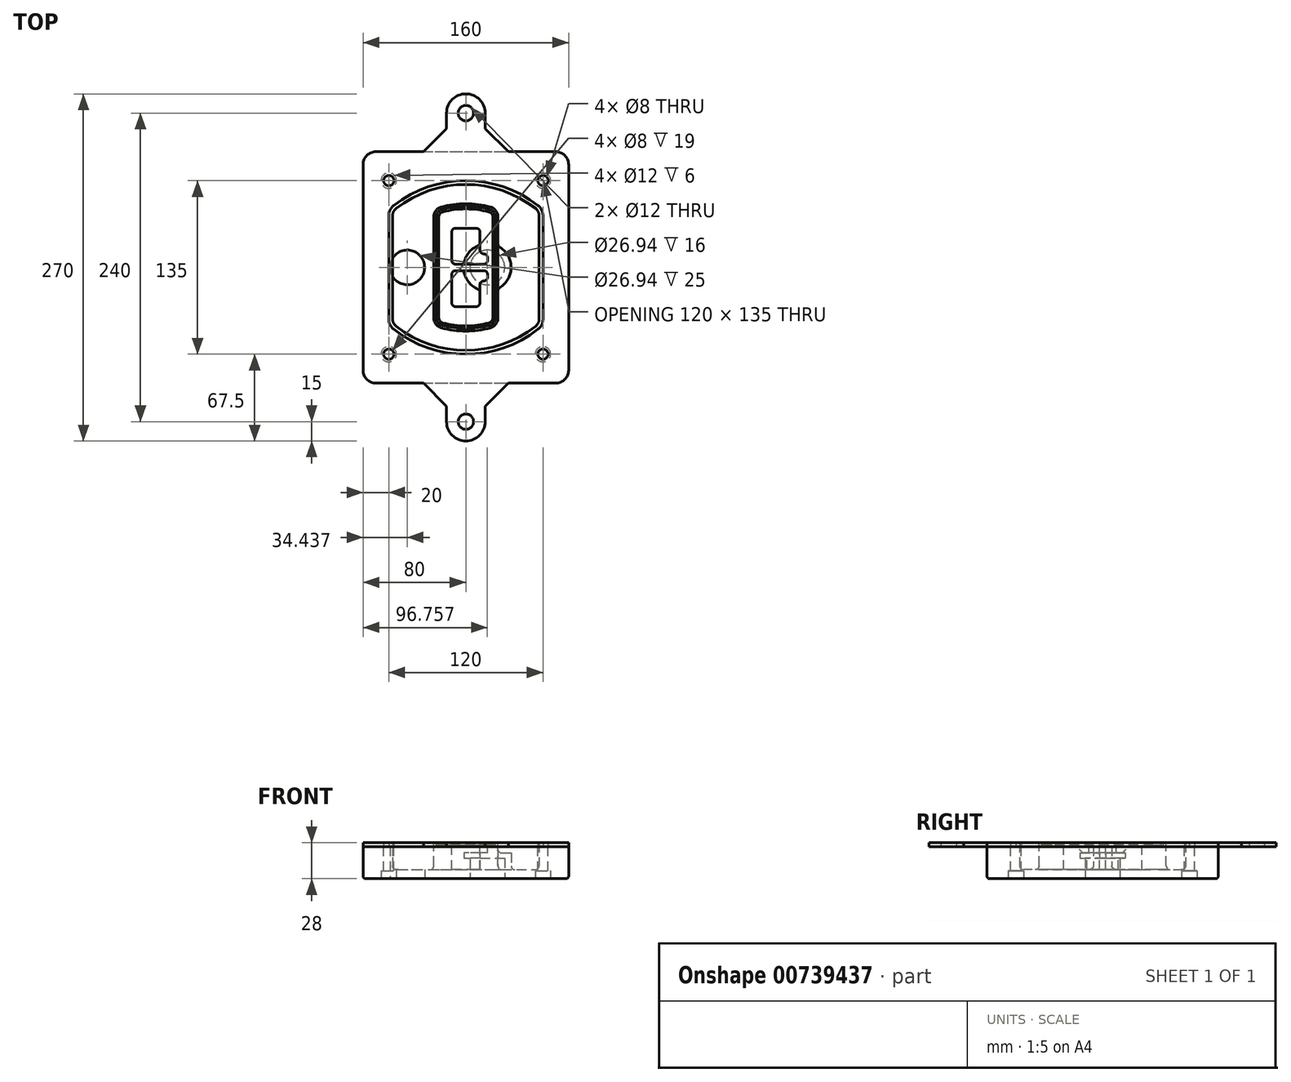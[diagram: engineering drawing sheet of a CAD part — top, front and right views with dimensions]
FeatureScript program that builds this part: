
annotation { "Feature Type Name" : "Feature", "Feature Type Description" : "" }
export const myFeature = defineFeature(function(context is Context, id is Id, definition is map)
    precondition{}
    {
        {
            var Q0;
            Q0=qCreatedBy(makeId("Top.planeOp"),FACE);
            var sketch = newSketch(context, id + "F0", { "sketchPlane" : qUnion([Q0])});
            skPoint(sketch, "E0.rect.middle", {"position": v(0, 0) * mm});
            skLineSegment(sketch, "E1.bottom", {"start": v(-70, -90) * mm, "end": v(70, -90) * mm});
            skLineSegment(sketch, "E1.top", {"start": v(-70, 90) * mm, "end": v(70, 90) * mm});
            skLineSegment(sketch, "E1.left", {"start": v(-80, -80) * mm, "end": v(-80, 80) * mm});
            skLineSegment(sketch, "E1.right", {"start": v(80, -80) * mm, "end": v(80, 80) * mm});
            skLineSegment(sketch, "E2", {"start": v(-80, 90) * mm, "end": v(80, -90) * mm, "construction": true});
            skLineSegment(sketch, "E3", {"start": v(80, 90) * mm, "end": v(-80, -90) * mm, "construction": true});
            skCircle(sketch, "E4", {"center": v(-60, 67.5) * mm, "radius": 4 * mm});
            skCircle(sketch, "E5", {"center": v(60, 67.5) * mm, "radius": 4 * mm});
            skCircle(sketch, "E6", {"center": v(60, -67.5) * mm, "radius": 4 * mm});
            skCircle(sketch, "E7", {"center": v(-60, -67.5) * mm, "radius": 4 * mm});
            skLineSegment(sketch, "E8", {"start": v(-60, 67.5) * mm, "end": v(60, 67.5) * mm, "construction": true});
            skLineSegment(sketch, "E9", {"start": v(60, 67.5) * mm, "end": v(60, -67.5) * mm, "construction": true});
            skLineSegment(sketch, "E10", {"start": v(60, -67.5) * mm, "end": v(-60, -67.5) * mm, "construction": true});
            skLineSegment(sketch, "E11", {"start": v(-60, -67.5) * mm, "end": v(-60, 67.5) * mm, "construction": true});
            skLineSegment(sketch, "E12", {"start": v(-60, 40.3) * mm, "end": v(-60, -40.3) * mm});
            skLineSegment(sketch, "E13", {"start": v(60, 40.3) * mm, "end": v(60, -40.3) * mm});
            skArc(sketch, "E14", {"start": v(56.15, 48.18) * mm, "mid": v(0, 67.5) * mm, "end": v(-56.15, 48.18) * mm});
            skArc(sketch, "E15", {"start": v(-56.15, -48.18) * mm, "mid": v(0, -67.5) * mm, "end": v(56.15, -48.18) * mm});
            skLineSegment(sketch, "E16", {"start": v(-60, 0) * mm, "end": v(60, 0) * mm, "construction": true});
            skPoint(sketch, "E17.visualSharp", {"position": v(-60, -45) * mm});
            skArc(sketch, "E17.filletArc", {"start": v(-60, -40.3) * mm, "mid": v(-58.99, -44.68) * mm, "end": v(-56.15, -48.18) * mm});
            skPoint(sketch, "E18.visualSharp", {"position": v(-60, 45) * mm});
            skArc(sketch, "E18.filletArc", {"start": v(-56.15, 48.18) * mm, "mid": v(-58.99, 44.68) * mm, "end": v(-60, 40.3) * mm});
            skPoint(sketch, "E19.visualSharp", {"position": v(60, 45) * mm});
            skArc(sketch, "E19.filletArc", {"start": v(60, 40.3) * mm, "mid": v(58.99, 44.68) * mm, "end": v(56.15, 48.18) * mm});
            skPoint(sketch, "E20.visualSharp", {"position": v(60, -45) * mm});
            skArc(sketch, "E20.filletArc", {"start": v(56.15, -48.18) * mm, "mid": v(58.99, -44.68) * mm, "end": v(60, -40.3) * mm});
            skPoint(sketch, "E21.visualSharp", {"position": v(-80, 90) * mm});
            skArc(sketch, "E21.filletArc", {"start": v(-70, 90) * mm, "mid": v(-77.07, 87.07) * mm, "end": v(-80, 80) * mm});
            skPoint(sketch, "E22.visualSharp", {"position": v(80, 90) * mm});
            skArc(sketch, "E22.filletArc", {"start": v(80, 80) * mm, "mid": v(77.07, 87.07) * mm, "end": v(70, 90) * mm});
            skPoint(sketch, "E23.visualSharp", {"position": v(80, -90) * mm});
            skArc(sketch, "E23.filletArc", {"start": v(70, -90) * mm, "mid": v(77.07, -87.07) * mm, "end": v(80, -80) * mm});
            skPoint(sketch, "E24.visualSharp", {"position": v(-80, -90) * mm});
            skArc(sketch, "E24.filletArc", {"start": v(-80, -80) * mm, "mid": v(-77.07, -87.07) * mm, "end": v(-70, -90) * mm});
            skArc(sketch, "E25.0", {"start": v(57, 40.3) * mm, "mid": v(56.3, 43.36) * mm, "end": v(54.3, 45.81) * mm});
            skLineSegment(sketch, "E25.1", {"start": v(57, 40.3) * mm, "end": v(57, -40.3) * mm});
            skArc(sketch, "E25.2", {"start": v(54.3, -45.81) * mm, "mid": v(56.3, -43.36) * mm, "end": v(57, -40.3) * mm});
            skArc(sketch, "E25.3", {"start": v(-54.3, -45.81) * mm, "mid": v(0, -64.5) * mm, "end": v(54.3, -45.81) * mm});
            skArc(sketch, "E25.4", {"start": v(-57, -40.3) * mm, "mid": v(-56.3, -43.36) * mm, "end": v(-54.3, -45.81) * mm});
            skArc(sketch, "E25.5", {"start": v(54.3, 45.81) * mm, "mid": v(0, 64.5) * mm, "end": v(-54.3, 45.81) * mm});
            skLineSegment(sketch, "E25.6", {"start": v(-57, 40.3) * mm, "end": v(-57, -40.3) * mm});
            skArc(sketch, "E25.7", {"start": v(-54.3, 45.81) * mm, "mid": v(-56.3, 43.36) * mm, "end": v(-57, 40.3) * mm});
            skArc(sketch, "E26.0", {"start": v(-58.62, 51.33) * mm, "mid": v(-62.58, 46.43) * mm, "end": v(-64, 40.3) * mm});
            skArc(sketch, "E26.1", {"start": v(58.62, 51.33) * mm, "mid": v(0, 71.5) * mm, "end": v(-58.62, 51.33) * mm});
            skArc(sketch, "E26.2", {"start": v(64, 40.3) * mm, "mid": v(62.58, 46.43) * mm, "end": v(58.62, 51.33) * mm});
            skLineSegment(sketch, "E26.3", {"start": v(64, 40.3) * mm, "end": v(64, -40.3) * mm});
            skArc(sketch, "E26.4", {"start": v(58.62, -51.33) * mm, "mid": v(62.58, -46.43) * mm, "end": v(64, -40.3) * mm});
            skLineSegment(sketch, "E26.5", {"start": v(-64, 40.3) * mm, "end": v(-64, -40.3) * mm});
            skArc(sketch, "E26.6", {"start": v(-58.62, -51.33) * mm, "mid": v(0, -71.5) * mm, "end": v(58.62, -51.33) * mm});
            skArc(sketch, "E26.7", {"start": v(-64, -40.3) * mm, "mid": v(-62.58, -46.43) * mm, "end": v(-58.62, -51.33) * mm});
            skSolve(sketch);
        }
        {
            var Q0;
            Q0=makeQuery(id+"F0.imprint","IMPRINT",FACE,{"disambiguationData":[TD([[makeQuery(id+"F0.imprint","IMPRINT",EDGE,{"derivedFrom":sQuery(id+"F0.wireOp",EDGE,"E1.bottom")}),1.0]])]});
            var Q1;
            Q1=makeQuery(id+"F0.imprint","IMPRINT",FACE,{"disambiguationData":[TD([[makeQuery(id+"F0.imprint","IMPRINT",EDGE,{"derivedFrom":sQuery(id+"F0.wireOp",EDGE,"E12")}),1.0]])]});
            var Q2;
            Q2=makeQuery(id+"F0.imprint","IMPRINT",FACE,{"disambiguationData":[TD([[makeQuery(id+"F0.imprint","IMPRINT",EDGE,{"derivedFrom":sQuery(id+"F0.wireOp",EDGE,"E25.0")}),1.0]])]});
            var Q3;
            Q3=makeQuery(id+"F0.imprint","IMPRINT",FACE,{"disambiguationData":[TD([[makeQuery(id+"F0.imprint","IMPRINT",EDGE,{"derivedFrom":sQuery(id+"F0.wireOp",EDGE,"E12")}),-1.0]])]});
            extrude(context, id + "F1", {"entities" : qUnion([Q0, Q1, Q2, Q3]), "oppositeDirection" : true, "depth" : 25 * mm});
        }
        {
            var Q0;
            Q0=makeQuery(id+"F0.imprint","IMPRINT",FACE,{"disambiguationData":[TD([[makeQuery(id+"F0.imprint","IMPRINT",EDGE,{"derivedFrom":sQuery(id+"F0.wireOp",EDGE,"E12")}),1.0]])]});
            extrude(context, id + "F2", {"entities" : qUnion([Q0]), "operationType" : NewBodyOperationType.ADD, "depth" : 3 * mm});
        }
        {
            var Q0;
            Q0=makeQuery(id+"F0.imprint","IMPRINT",FACE,{"disambiguationData":[TD([[makeQuery(id+"F0.imprint","IMPRINT",EDGE,{"derivedFrom":sQuery(id+"F0.wireOp",EDGE,"E25.0")}),1.0]])]});
            extrude(context, id + "F3", {"entities" : qUnion([Q0]), "operationType" : NewBodyOperationType.REMOVE, "oppositeDirection" : true, "depth" : 18 * mm});
        }
        {
            var Q0;
            Q0=makeQuery(id+"F2.opExtrude","CAP_FACE",FACE,{"disambiguationData":[OSD([sQuery(id+"F0.wireOp",EDGE,"E12"),sQuery(id+"F0.wireOp",EDGE,"E13"),sQuery(id+"F0.wireOp",EDGE,"E14"),sQuery(id+"F0.wireOp",EDGE,"E15"),sQuery(id+"F0.wireOp",EDGE,"E17.filletArc"),sQuery(id+"F0.wireOp",EDGE,"E18.filletArc"),sQuery(id+"F0.wireOp",EDGE,"E19.filletArc"),sQuery(id+"F0.wireOp",EDGE,"E20.filletArc"),sQuery(id+"F0.wireOp",EDGE,"E25.0"),sQuery(id+"F0.wireOp",EDGE,"E25.1"),sQuery(id+"F0.wireOp",EDGE,"E25.2"),sQuery(id+"F0.wireOp",EDGE,"E25.3"),sQuery(id+"F0.wireOp",EDGE,"E25.4"),sQuery(id+"F0.wireOp",EDGE,"E25.5"),sQuery(id+"F0.wireOp",EDGE,"E25.6"),sQuery(id+"F0.wireOp",EDGE,"E25.7")])],"isStart":false});
            var sketch = newSketch(context, id + "F4", { "sketchPlane" : qUnion([Q0])});
            skArc(sketch, "E27.0", {"start": v(-19.08, -46.97) * mm, "mid": v(0, -49.5) * mm, "end": v(19.08, -46.97) * mm});
            skArc(sketch, "E28.0", {"start": v(19.08, 46.97) * mm, "mid": v(0, 49.5) * mm, "end": v(-19.08, 46.97) * mm});
            skLineSegment(sketch, "E29", {"start": v(-25, 39.25) * mm, "end": v(-25, -39.25) * mm});
            skLineSegment(sketch, "E30", {"start": v(25, 39.25) * mm, "end": v(25, -39.25) * mm});
            skLineSegment(sketch, "E31", {"start": v(-25, 45.1) * mm, "end": v(25, 45.1) * mm, "construction": true});
            skLineSegment(sketch, "E32", {"start": v(-25, -45.1) * mm, "end": v(25, -45.1) * mm, "construction": true});
            skPoint(sketch, "E33.visualSharp", {"position": v(-25, 45.1) * mm});
            skArc(sketch, "E33.filletArc", {"start": v(-19.08, 46.97) * mm, "mid": v(-23.35, 44.11) * mm, "end": v(-25, 39.25) * mm});
            skPoint(sketch, "E34.visualSharp", {"position": v(25, 45.1) * mm});
            skArc(sketch, "E34.filletArc", {"start": v(25, 39.25) * mm, "mid": v(23.35, 44.11) * mm, "end": v(19.08, 46.97) * mm});
            skPoint(sketch, "E35.visualSharp", {"position": v(25, -45.1) * mm});
            skArc(sketch, "E35.filletArc", {"start": v(19.08, -46.97) * mm, "mid": v(23.35, -44.11) * mm, "end": v(25, -39.25) * mm});
            skPoint(sketch, "E36.visualSharp", {"position": v(-25, -45.1) * mm});
            skArc(sketch, "E36.filletArc", {"start": v(-25, -39.25) * mm, "mid": v(-23.35, -44.11) * mm, "end": v(-19.08, -46.97) * mm});
            skArc(sketch, "E37.0", {"start": v(54.3, 45.81) * mm, "mid": v(0, 64.5) * mm, "end": v(-54.3, 45.81) * mm});
            skArc(sketch, "E37.1", {"start": v(-54.3, 45.81) * mm, "mid": v(-56.3, 43.36) * mm, "end": v(-57, 40.3) * mm});
            skLineSegment(sketch, "E37.2", {"start": v(-57, 40.3) * mm, "end": v(-57, -40.3) * mm});
            skArc(sketch, "E37.3", {"start": v(-57, -40.3) * mm, "mid": v(-56.3, -43.36) * mm, "end": v(-54.3, -45.81) * mm});
            skArc(sketch, "E37.4", {"start": v(-54.3, -45.81) * mm, "mid": v(0, -64.5) * mm, "end": v(54.3, -45.81) * mm});
            skArc(sketch, "E37.5", {"start": v(54.3, -45.81) * mm, "mid": v(56.3, -43.36) * mm, "end": v(57, -40.3) * mm});
            skLineSegment(sketch, "E37.6", {"start": v(57, 40.3) * mm, "end": v(57, -40.3) * mm});
            skArc(sketch, "E37.7", {"start": v(57, 40.3) * mm, "mid": v(56.3, 43.36) * mm, "end": v(54.3, 45.81) * mm});
            skLineSegment(sketch, "E38.0", {"start": v(23, 39.25) * mm, "end": v(23, -39.25) * mm});
            skArc(sketch, "E38.1", {"start": v(18.56, -45.04) * mm, "mid": v(21.76, -42.9) * mm, "end": v(23, -39.25) * mm});
            skArc(sketch, "E38.2", {"start": v(-18.56, -45.04) * mm, "mid": v(0, -47.5) * mm, "end": v(18.56, -45.04) * mm});
            skArc(sketch, "E38.3", {"start": v(-23, -39.25) * mm, "mid": v(-21.76, -42.9) * mm, "end": v(-18.56, -45.04) * mm});
            skLineSegment(sketch, "E38.4", {"start": v(-23, 39.25) * mm, "end": v(-23, -39.25) * mm});
            skArc(sketch, "E38.5", {"start": v(23, 39.25) * mm, "mid": v(21.76, 42.9) * mm, "end": v(18.56, 45.04) * mm});
            skArc(sketch, "E38.6", {"start": v(-18.56, 45.04) * mm, "mid": v(-21.76, 42.9) * mm, "end": v(-23, 39.25) * mm});
            skArc(sketch, "E38.7", {"start": v(18.56, 45.04) * mm, "mid": v(0, 47.5) * mm, "end": v(-18.56, 45.04) * mm});
            skArc(sketch, "E39.0", {"start": v(21, 39.25) * mm, "mid": v(20.18, 41.68) * mm, "end": v(18.04, 43.1) * mm});
            skLineSegment(sketch, "E39.1", {"start": v(21, 39.25) * mm, "end": v(21, -39.25) * mm});
            skArc(sketch, "E39.2", {"start": v(18.04, -43.1) * mm, "mid": v(20.18, -41.68) * mm, "end": v(21, -39.25) * mm});
            skArc(sketch, "E39.3", {"start": v(-18.04, -43.1) * mm, "mid": v(0, -45.5) * mm, "end": v(18.04, -43.1) * mm});
            skArc(sketch, "E39.4", {"start": v(-21, -39.25) * mm, "mid": v(-20.18, -41.68) * mm, "end": v(-18.04, -43.1) * mm});
            skArc(sketch, "E39.5", {"start": v(18.04, 43.1) * mm, "mid": v(0, 45.5) * mm, "end": v(-18.04, 43.1) * mm});
            skLineSegment(sketch, "E39.6", {"start": v(-21, 39.25) * mm, "end": v(-21, -39.25) * mm});
            skArc(sketch, "E39.7", {"start": v(-18.04, 43.1) * mm, "mid": v(-20.18, 41.68) * mm, "end": v(-21, 39.25) * mm});
            skLineSegment(sketch, "E40", {"start": v(-25, 0) * mm, "end": v(25, 0) * mm, "construction": true});
            skLineSegment(sketch, "E41", {"start": v(-11, 5.5) * mm, "end": v(-11, 27.5) * mm});
            skLineSegment(sketch, "E42", {"start": v(-8, 30.5) * mm, "end": v(8, 30.5) * mm});
            skLineSegment(sketch, "E43", {"start": v(11, 27.5) * mm, "end": v(11, 13.5) * mm});
            skLineSegment(sketch, "E44", {"start": v(14, 10.5) * mm, "end": v(14, 10.5) * mm});
            skLineSegment(sketch, "E45", {"start": v(17, 7.5) * mm, "end": v(17, 5.5) * mm});
            skLineSegment(sketch, "E46", {"start": v(14, 2.5) * mm, "end": v(-8, 2.5) * mm});
            skPoint(sketch, "E47.visualSharp", {"position": v(-11, 30.5) * mm});
            skArc(sketch, "E47.filletArc", {"start": v(-8, 30.5) * mm, "mid": v(-10.12, 29.62) * mm, "end": v(-11, 27.5) * mm});
            skPoint(sketch, "E48.visualSharp", {"position": v(11, 30.5) * mm});
            skArc(sketch, "E48.filletArc", {"start": v(11, 27.5) * mm, "mid": v(10.12, 29.62) * mm, "end": v(8, 30.5) * mm});
            skPoint(sketch, "E49.visualSharp", {"position": v(11, 10.5) * mm});
            skArc(sketch, "E49.filletArc", {"start": v(11, 13.5) * mm, "mid": v(11.88, 11.38) * mm, "end": v(14, 10.5) * mm});
            skPoint(sketch, "E50.visualSharp", {"position": v(17, 10.5) * mm});
            skArc(sketch, "E50.filletArc", {"start": v(17, 7.5) * mm, "mid": v(16.12, 9.62) * mm, "end": v(14, 10.5) * mm});
            skPoint(sketch, "E51.visualSharp", {"position": v(17, 2.5) * mm});
            skArc(sketch, "E51.filletArc", {"start": v(14, 2.5) * mm, "mid": v(16.12, 3.38) * mm, "end": v(17, 5.5) * mm});
            skPoint(sketch, "E52.visualSharp", {"position": v(-11, 2.5) * mm});
            skArc(sketch, "E52.filletArc", {"start": v(-11, 5.5) * mm, "mid": v(-10.12, 3.38) * mm, "end": v(-8, 2.5) * mm});
            skLineSegment(sketch, "E53.0.MirrorCS", {"start": v(14, -2.5) * mm, "end": v(-8, -2.5) * mm});
            skArc(sketch, "E54.0.MirrorCS", {"start": v(-11, -5.5) * mm, "mid": v(-10.12, -3.38) * mm, "end": v(-8, -2.5) * mm});
            skLineSegment(sketch, "E55.0.MirrorCS", {"start": v(-11, -5.5) * mm, "end": v(-11, -27.5) * mm});
            skArc(sketch, "E56.0.MirrorCS", {"start": v(-8, -30.5) * mm, "mid": v(-10.12, -29.62) * mm, "end": v(-11, -27.5) * mm});
            skLineSegment(sketch, "E57.0.MirrorCS", {"start": v(-8, -30.5) * mm, "end": v(8, -30.5) * mm});
            skArc(sketch, "E58.0.MirrorCS", {"start": v(11, -27.5) * mm, "mid": v(10.12, -29.62) * mm, "end": v(8, -30.5) * mm});
            skLineSegment(sketch, "E59.0.MirrorCS", {"start": v(11, -27.5) * mm, "end": v(11, -13.5) * mm});
            skArc(sketch, "E60.0.MirrorCS", {"start": v(11, -13.5) * mm, "mid": v(11.88, -11.38) * mm, "end": v(14, -10.5) * mm});
            skArc(sketch, "E61.0.MirrorCS", {"start": v(17, -7.5) * mm, "mid": v(16.12, -9.62) * mm, "end": v(14, -10.5) * mm});
            skLineSegment(sketch, "E62.0.MirrorCS", {"start": v(17, -7.5) * mm, "end": v(17, -5.5) * mm});
            skArc(sketch, "E63.0.MirrorCS", {"start": v(14, -2.5) * mm, "mid": v(16.12, -3.38) * mm, "end": v(17, -5.5) * mm});
            skSolve(sketch);
        }
        {
            var Q0;
            Q0=makeQuery(id+"F4.imprint","IMPRINT",FACE,{"disambiguationData":[TD([[makeQuery(id+"F4.imprint","IMPRINT",EDGE,{"derivedFrom":sQuery(id+"F4.wireOp",EDGE,"E27.0")}),1.0]])]});
            var Q1;
            Q1=makeQuery(id+"F4.imprint","IMPRINT",FACE,{"disambiguationData":[TD([[makeQuery(id+"F4.imprint","IMPRINT",EDGE,{"derivedFrom":sQuery(id+"F4.wireOp",EDGE,"E38.0")}),-1.0]])]});
            var Q2;
            Q2=makeQuery(id+"F4.imprint","IMPRINT",FACE,{"disambiguationData":[TD([[makeQuery(id+"F4.imprint","IMPRINT",EDGE,{"derivedFrom":sQuery(id+"F4.wireOp",EDGE,"E39.0")}),1.0]])]});
            extrude(context, id + "F5", {"entities" : qUnion([Q0, Q1, Q2]), "operationType" : NewBodyOperationType.ADD, "endBound" : BoundingType.UP_TO_NEXT, "oppositeDirection" : true, "depth" : 25 * mm});
        }
        {
            var Q0;
            Q0=makeQuery(id+"F4.imprint","IMPRINT",FACE,{"disambiguationData":[TD([[makeQuery(id+"F4.imprint","IMPRINT",EDGE,{"derivedFrom":sQuery(id+"F4.wireOp",EDGE,"E38.0")}),-1.0]])]});
            extrude(context, id + "F6", {"entities" : qUnion([Q0]), "operationType" : NewBodyOperationType.REMOVE, "oppositeDirection" : true, "depth" : 2 * mm});
        }
        {
            var Q0;
            Q0=makeQuery(id+"F1.opExtrude","CAP_FACE",FACE,{"disambiguationData":[OSD([sQuery(id+"F0.wireOp",EDGE,"E1.bottom"),sQuery(id+"F0.wireOp",EDGE,"E1.top"),sQuery(id+"F0.wireOp",EDGE,"E1.left"),sQuery(id+"F0.wireOp",EDGE,"E1.right"),sQuery(id+"F0.wireOp",EDGE,"E4"),sQuery(id+"F0.wireOp",EDGE,"E5"),sQuery(id+"F0.wireOp",EDGE,"E6"),sQuery(id+"F0.wireOp",EDGE,"E7"),sQuery(id+"F0.wireOp",EDGE,"E21.filletArc"),sQuery(id+"F0.wireOp",EDGE,"E22.filletArc"),sQuery(id+"F0.wireOp",EDGE,"E23.filletArc"),sQuery(id+"F0.wireOp",EDGE,"E24.filletArc")])],"isStart":false});
            var sketch = newSketch(context, id + "F7", { "sketchPlane" : qUnion([Q0])});
            skCircle(sketch, "E64", {"center": v(16.76, 0) * mm, "radius": 13.47 * mm});
            skCircle(sketch, "E65", {"center": v(-45.56, 0) * mm, "radius": 13.47 * mm});
            skLineSegment(sketch, "E66", {"start": v(80, 0) * mm, "end": v(-80, 0) * mm});
            skCircle(sketch, "E67", {"center": v(16.76, 0) * mm, "radius": 18.47 * mm});
            skCircle(sketch, "E68", {"center": v(60, -67.5) * mm, "radius": 6 * mm});
            skCircle(sketch, "E69", {"center": v(-60, -67.5) * mm, "radius": 6 * mm});
            skCircle(sketch, "E70", {"center": v(-60, 67.5) * mm, "radius": 6 * mm});
            skCircle(sketch, "E71", {"center": v(60, 67.5) * mm, "radius": 6 * mm});
            skSolve(sketch);
        }
        {
            var Q0;
            {var subQ1=sQuery(id+"F7.wireOp",EDGE,"E66");var subQ4=sQuery(id+"F7.wireOp",EDGE,"E64");var subQ6=makeQuery(id+"F7.imprint","INTERSECT",VERTEX,{"disambiguationData":[OD(0.0)],"derivedFrom":[subQ4,subQ1]});Q0=makeQuery(id+"F7.imprint","IMPRINT",FACE,{"disambiguationData":[TD([[makeQuery(id+"F7.imprint","IMPRINT",EDGE,{"disambiguationData":[TD([[subQ6,-1.0]])],"derivedFrom":subQ4}),-1.0]])]});}
            var Q1;
            {var subQ0=sQuery(id+"F7.wireOp",EDGE,"E66");var subQ1=sQuery(id+"F7.wireOp",EDGE,"E64");var subQ3=makeQuery(id+"F7.imprint","INTERSECT",VERTEX,{"disambiguationData":[OD(0.0)],"derivedFrom":[subQ1,subQ0]});Q1=makeQuery(id+"F7.imprint","IMPRINT",FACE,{"disambiguationData":[TD([[makeQuery(id+"F7.imprint","IMPRINT",EDGE,{"disambiguationData":[TD([[subQ3,-1.0]])],"derivedFrom":subQ1}),1.0]])]});}
            var Q2;
            {var subQ0=sQuery(id+"F7.wireOp",EDGE,"E66");var subQ1=sQuery(id+"F7.wireOp",EDGE,"E64");var subQ3=makeQuery(id+"F7.imprint","INTERSECT",VERTEX,{"disambiguationData":[OD(0.0)],"derivedFrom":[subQ1,subQ0]});Q2=makeQuery(id+"F7.imprint","IMPRINT",FACE,{"disambiguationData":[TD([[makeQuery(id+"F7.imprint","IMPRINT",EDGE,{"disambiguationData":[TD([[subQ3,1.0]])],"derivedFrom":subQ1}),1.0]])]});}
            var Q3;
            {var subQ1=sQuery(id+"F7.wireOp",EDGE,"E66");var subQ4=sQuery(id+"F7.wireOp",EDGE,"E64");var subQ6=makeQuery(id+"F7.imprint","INTERSECT",VERTEX,{"disambiguationData":[OD(0.0)],"derivedFrom":[subQ4,subQ1]});Q3=makeQuery(id+"F7.imprint","IMPRINT",FACE,{"disambiguationData":[TD([[makeQuery(id+"F7.imprint","IMPRINT",EDGE,{"disambiguationData":[TD([[subQ6,1.0]])],"derivedFrom":subQ4}),-1.0]])]});}
            extrude(context, id + "F8", {"entities" : qUnion([Q0, Q1, Q2, Q3]), "operationType" : NewBodyOperationType.ADD, "oppositeDirection" : true, "depth" : 20 * mm});
        }
        {
            var Q0;
            {var subQ0=sQuery(id+"F7.wireOp",EDGE,"E66");var subQ1=sQuery(id+"F7.wireOp",EDGE,"E64");var subQ3=makeQuery(id+"F7.imprint","INTERSECT",VERTEX,{"disambiguationData":[OD(0.0)],"derivedFrom":[subQ1,subQ0]});Q0=makeQuery(id+"F7.imprint","IMPRINT",FACE,{"disambiguationData":[TD([[makeQuery(id+"F7.imprint","IMPRINT",EDGE,{"disambiguationData":[TD([[subQ3,-1.0]])],"derivedFrom":subQ1}),1.0]])]});}
            var Q1;
            {var subQ0=sQuery(id+"F7.wireOp",EDGE,"E66");var subQ1=sQuery(id+"F7.wireOp",EDGE,"E64");var subQ3=makeQuery(id+"F7.imprint","INTERSECT",VERTEX,{"disambiguationData":[OD(0.0)],"derivedFrom":[subQ1,subQ0]});Q1=makeQuery(id+"F7.imprint","IMPRINT",FACE,{"disambiguationData":[TD([[makeQuery(id+"F7.imprint","IMPRINT",EDGE,{"disambiguationData":[TD([[subQ3,1.0]])],"derivedFrom":subQ1}),1.0]])]});}
            extrude(context, id + "F9", {"entities" : qUnion([Q0, Q1]), "operationType" : NewBodyOperationType.REMOVE, "oppositeDirection" : true, "depth" : 16 * mm});
        }
        {
            var Q0;
            {var subQ0=sQuery(id+"F7.wireOp",EDGE,"E66");var subQ1=sQuery(id+"F7.wireOp",EDGE,"E65");var subQ3=makeQuery(id+"F7.imprint","INTERSECT",VERTEX,{"disambiguationData":[OD(0.0)],"derivedFrom":[subQ1,subQ0]});Q0=makeQuery(id+"F7.imprint","IMPRINT",FACE,{"disambiguationData":[TD([[makeQuery(id+"F7.imprint","IMPRINT",EDGE,{"disambiguationData":[TD([[subQ3,-1.0]])],"derivedFrom":subQ1}),1.0]])]});}
            var Q1;
            {var subQ0=sQuery(id+"F7.wireOp",EDGE,"E66");var subQ1=sQuery(id+"F7.wireOp",EDGE,"E65");var subQ3=makeQuery(id+"F7.imprint","INTERSECT",VERTEX,{"disambiguationData":[OD(0.0)],"derivedFrom":[subQ1,subQ0]});Q1=makeQuery(id+"F7.imprint","IMPRINT",FACE,{"disambiguationData":[TD([[makeQuery(id+"F7.imprint","IMPRINT",EDGE,{"disambiguationData":[TD([[subQ3,1.0]])],"derivedFrom":subQ1}),1.0]])]});}
            extrude(context, id + "F10", {"entities" : qUnion([Q0, Q1]), "operationType" : NewBodyOperationType.REMOVE, "oppositeDirection" : true, "depth" : 25 * mm});
        }
        {
            var Q0;
            Q0=makeQuery(id+"F7.imprint","IMPRINT",FACE,{"disambiguationData":[TD([[makeQuery(id+"F7.imprint","IMPRINT",EDGE,{"derivedFrom":sQuery(id+"F7.wireOp",EDGE,"E68")}),1.0]])]});
            var Q1;
            Q1=makeQuery(id+"F7.imprint","IMPRINT",FACE,{"disambiguationData":[TD([[makeQuery(id+"F7.imprint","IMPRINT",EDGE,{"derivedFrom":makeQuery(id+"F1.opExtrude","CAP_EDGE",EDGE,{"disambiguationData":[OSD([sQuery(id+"F0.wireOp",EDGE,"E5")])],"isStart":false})}),-1.0]])]});
            var Q2;
            Q2=makeQuery(id+"F7.imprint","IMPRINT",FACE,{"disambiguationData":[TD([[makeQuery(id+"F7.imprint","IMPRINT",EDGE,{"derivedFrom":sQuery(id+"F7.wireOp",EDGE,"E69")}),1.0]])]});
            var Q3;
            Q3=makeQuery(id+"F7.imprint","IMPRINT",FACE,{"disambiguationData":[TD([[makeQuery(id+"F7.imprint","IMPRINT",EDGE,{"derivedFrom":makeQuery(id+"F1.opExtrude","CAP_EDGE",EDGE,{"disambiguationData":[OSD([sQuery(id+"F0.wireOp",EDGE,"E4")])],"isStart":false})}),-1.0]])]});
            var Q4;
            Q4=makeQuery(id+"F7.imprint","IMPRINT",FACE,{"disambiguationData":[TD([[makeQuery(id+"F7.imprint","IMPRINT",EDGE,{"derivedFrom":sQuery(id+"F7.wireOp",EDGE,"E70")}),1.0]])]});
            var Q5;
            Q5=makeQuery(id+"F7.imprint","IMPRINT",FACE,{"disambiguationData":[TD([[makeQuery(id+"F7.imprint","IMPRINT",EDGE,{"derivedFrom":makeQuery(id+"F1.opExtrude","CAP_EDGE",EDGE,{"disambiguationData":[OSD([sQuery(id+"F0.wireOp",EDGE,"E7")])],"isStart":false})}),-1.0]])]});
            var Q6;
            Q6=makeQuery(id+"F7.imprint","IMPRINT",FACE,{"disambiguationData":[TD([[makeQuery(id+"F7.imprint","IMPRINT",EDGE,{"derivedFrom":sQuery(id+"F7.wireOp",EDGE,"E71")}),1.0]])]});
            var Q7;
            Q7=makeQuery(id+"F7.imprint","IMPRINT",FACE,{"disambiguationData":[TD([[makeQuery(id+"F7.imprint","IMPRINT",EDGE,{"derivedFrom":makeQuery(id+"F1.opExtrude","CAP_EDGE",EDGE,{"disambiguationData":[OSD([sQuery(id+"F0.wireOp",EDGE,"E6")])],"isStart":false})}),-1.0]])]});
            extrude(context, id + "F11", {"entities" : qUnion([Q0, Q1, Q2, Q3, Q4, Q5, Q6, Q7]), "operationType" : NewBodyOperationType.REMOVE, "oppositeDirection" : true, "depth" : 6 * mm});
        }
        {
            var Q0;
            Q0=makeQuery(id+"F9.boolean.opBoolean","COPY",FACE,{"derivedFrom":makeQuery(id+"F9.opExtrude","CAP_FACE",FACE,{"disambiguationData":[OSD([sQuery(id+"F7.wireOp",EDGE,"E64")])],"isStart":false})});
            var sketch = newSketch(context, id + "F12", { "sketchPlane" : qUnion([Q0])});
            skArc(sketch, "E72.0", {"start": v(11, 17.55) * mm, "mid": v(2.57, 11.82) * mm, "end": v(-1.54, 2.5) * mm});
            skArc(sketch, "E72.1", {"start": v(-1.54, -2.5) * mm, "mid": v(2.57, -11.82) * mm, "end": v(11, -17.55) * mm});
            skLineSegment(sketch, "E73", {"start": v(-1.54, -2.5) * mm, "end": v(14, -2.5) * mm});
            skLineSegment(sketch, "E74.0", {"start": v(14, 2.5) * mm, "end": v(-1.54, 2.5) * mm});
            skArc(sketch, "E74.1", {"start": v(14, 2.5) * mm, "mid": v(16.12, 3.38) * mm, "end": v(17, 5.5) * mm});
            skLineSegment(sketch, "E74.2", {"start": v(17, 7.5) * mm, "end": v(17, 5.5) * mm});
            skArc(sketch, "E74.3", {"start": v(17, 7.5) * mm, "mid": v(16.12, 9.62) * mm, "end": v(14, 10.5) * mm});
            skArc(sketch, "E74.4", {"start": v(11, 13.5) * mm, "mid": v(11.88, 11.38) * mm, "end": v(14, 10.5) * mm});
            skLineSegment(sketch, "E74.5", {"start": v(11, 17.55) * mm, "end": v(11, 13.5) * mm});
            skLineSegment(sketch, "E74.7", {"start": v(14, -2.5) * mm, "end": v(-1.54, -2.5) * mm});
            skArc(sketch, "E74.8", {"start": v(14, -2.5) * mm, "mid": v(16.12, -3.38) * mm, "end": v(17, -5.5) * mm});
            skLineSegment(sketch, "E74.9", {"start": v(17, -7.5) * mm, "end": v(17, -5.5) * mm});
            skArc(sketch, "E74.10", {"start": v(17, -7.5) * mm, "mid": v(16.12, -9.62) * mm, "end": v(14, -10.5) * mm});
            skArc(sketch, "E74.11", {"start": v(11, -13.5) * mm, "mid": v(11.88, -11.38) * mm, "end": v(14, -10.5) * mm});
            skLineSegment(sketch, "E74.12", {"start": v(11, -17.55) * mm, "end": v(11, -13.5) * mm});
            skPoint(sketch, "E75.orphan", {"position": v(11, -27.5) * mm});
            skPoint(sketch, "E76.orphan", {"position": v(-8, -2.5) * mm});
            skPoint(sketch, "E77.orphan", {"position": v(-8, 2.5) * mm});
            skPoint(sketch, "E78.orphan", {"position": v(11, 27.5) * mm});
            skSolve(sketch);
        }
        {
            var Q0;
            {var subQ7=sQuery(id+"F12.wireOp",EDGE,"E72.0");var subQ14=sQuery(id+"F12.wireOp",EDGE,"E72.1");var subQ16=sQuery(id+"F12.wireOp",EDGE,"E74.1");var subQ18=sQuery(id+"F12.wireOp",EDGE,"E74.8");Q0=qUnion([makeQuery(id+"F12.imprint","IMPRINT",FACE,{"disambiguationData":[TD([[makeQuery(id+"F12.imprint","IMPRINT",EDGE,{"derivedFrom":subQ7}),1.0]])]}),makeQuery(id+"F12.imprint","IMPRINT",FACE,{"disambiguationData":[TD([[makeQuery(id+"F12.imprint","IMPRINT",EDGE,{"derivedFrom":subQ14}),1.0]])]}),makeQuery(id+"F12.imprint","IMPRINT",FACE,{"disambiguationData":[TD([[makeQuery(id+"F12.imprint","IMPRINT",EDGE,{"derivedFrom":subQ16}),1.0]])]}),makeQuery(id+"F12.imprint","IMPRINT",FACE,{"disambiguationData":[TD([[makeQuery(id+"F12.imprint","IMPRINT",EDGE,{"derivedFrom":subQ18}),-1.0]])]})]);}
            var Q1;
            Q1=makeQuery(id+"F5.boolean.opBoolean","SPLIT",FACE,{"disambiguationData":[TD([makeQuery(id+"F5.opExtrude","SWEPT_FACE",FACE,{"disambiguationData":[OSD([sQuery(id+"F4.wireOp",EDGE,"E41")])]})])],"derivedFrom":makeQuery(id+"F3.boolean.opBoolean","COPY",FACE,{"derivedFrom":makeQuery(id+"F3.opExtrude","CAP_FACE",FACE,{"disambiguationData":[OSD([sQuery(id+"F0.wireOp",EDGE,"E25.0"),sQuery(id+"F0.wireOp",EDGE,"E25.1"),sQuery(id+"F0.wireOp",EDGE,"E25.2"),sQuery(id+"F0.wireOp",EDGE,"E25.3"),sQuery(id+"F0.wireOp",EDGE,"E25.4"),sQuery(id+"F0.wireOp",EDGE,"E25.5"),sQuery(id+"F0.wireOp",EDGE,"E25.6"),sQuery(id+"F0.wireOp",EDGE,"E25.7")])],"isStart":false})})});
            extrude(context, id + "F13", {"entities" : qUnion([Q0]), "operationType" : NewBodyOperationType.REMOVE, "endBound" : BoundingType.UP_TO_SURFACE, "endBoundEntityFace" : qUnion([Q1]), "depth" : 25 * mm});
        }
        {
            var Q0;
            Q0=makeQuery(id+"F3.boolean.opBoolean","COPY",EDGE,{"derivedFrom":makeQuery(id+"F3.opExtrude","CAP_EDGE",EDGE,{"disambiguationData":[OSD([sQuery(id+"F0.wireOp",EDGE,"E25.6")])],"isStart":false})});
            var Q1;
            Q1=makeQuery(id+"F8.boolean.opBoolean","INTERSECT",EDGE,{"derivedFrom":[makeQuery(id+"F5.opExtrude","SWEPT_FACE",FACE,{"disambiguationData":[OSD([sQuery(id+"F4.wireOp",EDGE,"E30")])]}),makeQuery(id+"F8.opExtrude","CAP_FACE",FACE,{"disambiguationData":[OSD([sQuery(id+"F7.wireOp",EDGE,"E67")])],"isStart":false})]});
            var Q2;
            Q2=makeQuery(id+"F8.boolean.opBoolean","INTERSECT",EDGE,{"disambiguationData":[OD(1.0)],"derivedFrom":[makeQuery(id+"F5.opExtrude","SWEPT_FACE",FACE,{"disambiguationData":[OSD([sQuery(id+"F4.wireOp",EDGE,"E30")])]}),makeQuery(id+"F8.opExtrude","SWEPT_FACE",FACE,{"disambiguationData":[OSD([sQuery(id+"F7.wireOp",EDGE,"E67")])]})]});
            var Q3;
            {var subQ0=sQuery(id+"F4.wireOp",EDGE,"E30");Q3=makeQuery(id+"F8.boolean.opBoolean","SPLIT",EDGE,{"disambiguationData":[TD([makeQuery(id+"F5.opExtrude","SWEPT_FACE",FACE,{"disambiguationData":[OSD([sQuery(id+"F4.wireOp",EDGE,"E35.filletArc")])]})])],"derivedFrom":makeQuery(id+"F5.opExtrude","CAP_EDGE",EDGE,{"disambiguationData":[OSD([subQ0])],"isStart":false})});}
            var Q4;
            {var subQ0=sQuery(id+"F0.wireOp",EDGE,"E25.7");var subQ1=sQuery(id+"F0.wireOp",EDGE,"E25.1");var subQ2=sQuery(id+"F0.wireOp",EDGE,"E25.6");var subQ3=sQuery(id+"F0.wireOp",EDGE,"E25.5");var subQ4=sQuery(id+"F0.wireOp",EDGE,"E25.4");var subQ5=sQuery(id+"F0.wireOp",EDGE,"E25.0");var subQ6=sQuery(id+"F0.wireOp",EDGE,"E25.2");var subQ7=sQuery(id+"F0.wireOp",EDGE,"E25.3");Q4=makeQuery(id+"F8.boolean.opBoolean","INTERSECT",EDGE,{"derivedFrom":[makeQuery(id+"F5.boolean.opBoolean","SPLIT",FACE,{"disambiguationData":[TD([makeQuery(id+"F2.opExtrude","SWEPT_FACE",FACE,{"disambiguationData":[OSD([subQ5])]})])],"derivedFrom":makeQuery(id+"F3.boolean.opBoolean","COPY",FACE,{"derivedFrom":makeQuery(id+"F3.opExtrude","CAP_FACE",FACE,{"disambiguationData":[OSD([subQ5,subQ1,subQ6,subQ7,subQ4,subQ3,subQ2,subQ0])],"isStart":false})})}),makeQuery(id+"F8.opExtrude","SWEPT_FACE",FACE,{"disambiguationData":[OSD([sQuery(id+"F7.wireOp",EDGE,"E67")])]})]});}
            var Q5;
            Q5=makeQuery(id+"F8.boolean.opBoolean","INTERSECT",EDGE,{"disambiguationData":[OD(0.0)],"derivedFrom":[makeQuery(id+"F5.opExtrude","SWEPT_FACE",FACE,{"disambiguationData":[OSD([sQuery(id+"F4.wireOp",EDGE,"E30")])]}),makeQuery(id+"F8.opExtrude","SWEPT_FACE",FACE,{"disambiguationData":[OSD([sQuery(id+"F7.wireOp",EDGE,"E67")])]})]});
            fillet(context, id + "F14", {"entities" : qUnion([Q0, Q1, Q2, Q3, Q4, Q5]), "radius" : 3 * mm, "tangentPropagation" : true, "allowEdgeOverflow" : false});
        }
        {
            var Q0;
            Q0=makeQuery(id+"F1.opExtrude","CAP_EDGE",EDGE,{"disambiguationData":[OSD([sQuery(id+"F0.wireOp",EDGE,"E1.bottom")])],"isStart":false});
            fillet(context, id + "F15", {"entities" : qUnion([Q0]), "radius" : 2 * mm, "tangentPropagation" : true, "allowEdgeOverflow" : false});
        }
        {
            var Q0;
            {var subQ0=sQuery(id+"F0.wireOp",EDGE,"E21.filletArc");var subQ1=sQuery(id+"F0.wireOp",EDGE,"E7");var subQ2=sQuery(id+"F0.wireOp",EDGE,"E6");var subQ3=sQuery(id+"F0.wireOp",EDGE,"E5");var subQ4=sQuery(id+"F0.wireOp",EDGE,"E4");var subQ5=sQuery(id+"F0.wireOp",EDGE,"E22.filletArc");var subQ6=sQuery(id+"F0.wireOp",EDGE,"E1.bottom");var subQ7=sQuery(id+"F0.wireOp",EDGE,"E1.right");var subQ8=sQuery(id+"F0.wireOp",EDGE,"E1.top");var subQ9=sQuery(id+"F0.wireOp",EDGE,"E1.left");var subQ10=sQuery(id+"F0.wireOp",EDGE,"E23.filletArc");var subQ11=sQuery(id+"F0.wireOp",EDGE,"E24.filletArc");Q0=makeQuery(id+"F2.boolean.opBoolean","SPLIT",FACE,{"disambiguationData":[TD([makeQuery(id+"F1.opExtrude","SWEPT_FACE",FACE,{"disambiguationData":[OSD([subQ6])]})])],"derivedFrom":makeQuery(id+"F1.opExtrude","CAP_FACE",FACE,{"disambiguationData":[OSD([subQ6,subQ8,subQ9,subQ7,subQ4,subQ3,subQ2,subQ1,subQ0,subQ5,subQ10,subQ11])],"isStart":true})});}
            var sketch = newSketch(context, id + "F16", { "sketchPlane" : qUnion([Q0])});
            skLineSegment(sketch, "E79.0", {"start": v(-70, 90) * mm, "end": v(70, 90) * mm});
            skLineSegment(sketch, "E79.1", {"start": v(-80, -80) * mm, "end": v(-80, 80) * mm});
            skArc(sketch, "E79.2", {"start": v(-70, 90) * mm, "mid": v(-77.07, 87.07) * mm, "end": v(-80, 80) * mm});
            skCircle(sketch, "E79.3", {"center": v(-60, 67.5) * mm, "radius": 4 * mm});
            skArc(sketch, "E79.4", {"start": v(56.15, 48.18) * mm, "mid": v(0, 67.5) * mm, "end": v(-56.15, 48.18) * mm});
            skArc(sketch, "E79.5", {"start": v(-56.15, 48.18) * mm, "mid": v(-58.99, 44.68) * mm, "end": v(-60, 40.3) * mm});
            skLineSegment(sketch, "E79.6", {"start": v(-60, 40.3) * mm, "end": v(-60, -40.3) * mm});
            skArc(sketch, "E79.7", {"start": v(-60, -40.3) * mm, "mid": v(-58.99, -44.68) * mm, "end": v(-56.15, -48.18) * mm});
            skArc(sketch, "E79.8", {"start": v(-56.15, -48.18) * mm, "mid": v(0, -67.5) * mm, "end": v(56.15, -48.18) * mm});
            skCircle(sketch, "E79.9", {"center": v(-60, -67.5) * mm, "radius": 4 * mm});
            skCircle(sketch, "E79.10", {"center": v(60, 67.5) * mm, "radius": 4 * mm});
            skArc(sketch, "E79.11", {"start": v(80, 80) * mm, "mid": v(77.07, 87.07) * mm, "end": v(70, 90) * mm});
            skLineSegment(sketch, "E79.12", {"start": v(80, -80) * mm, "end": v(80, 80) * mm});
            skArc(sketch, "E79.13", {"start": v(60, 40.3) * mm, "mid": v(58.99, 44.68) * mm, "end": v(56.15, 48.18) * mm});
            skLineSegment(sketch, "E79.14", {"start": v(60, 40.3) * mm, "end": v(60, -40.3) * mm});
            skCircle(sketch, "E79.15", {"center": v(60, -67.5) * mm, "radius": 4 * mm});
            skArc(sketch, "E79.16", {"start": v(56.15, -48.18) * mm, "mid": v(58.99, -44.68) * mm, "end": v(60, -40.3) * mm});
            skArc(sketch, "E79.17", {"start": v(70, -90) * mm, "mid": v(77.07, -87.07) * mm, "end": v(80, -80) * mm});
            skLineSegment(sketch, "E79.18", {"start": v(-70, -90) * mm, "end": v(70, -90) * mm});
            skArc(sketch, "E79.19", {"start": v(-80, -80) * mm, "mid": v(-77.07, -87.07) * mm, "end": v(-70, -90) * mm});
            skLineSegment(sketch, "E80", {"start": v(-33, 90) * mm, "end": v(-15, 108) * mm});
            skLineSegment(sketch, "E81", {"start": v(33, 90) * mm, "end": v(15, 108) * mm});
            skLineSegment(sketch, "E82", {"start": v(-15, 108) * mm, "end": v(-15, 120) * mm});
            skLineSegment(sketch, "E83", {"start": v(15, 108) * mm, "end": v(15, 120) * mm});
            skLineSegment(sketch, "E84", {"start": v(0, 90) * mm, "end": v(0, 120) * mm, "construction": true});
            skCircle(sketch, "E85", {"center": v(0, 120) * mm, "radius": 6 * mm});
            skArc(sketch, "E86", {"start": v(15, 120) * mm, "mid": v(0, 135) * mm, "end": v(-15, 120) * mm});
            skLineSegment(sketch, "E87", {"start": v(-80, 0) * mm, "end": v(80, 0) * mm, "construction": true});
            skLineSegment(sketch, "E88", {"start": v(-80, 0) * mm, "end": v(80, 0) * mm});
            skLineSegment(sketch, "E89.MirrorCS", {"start": v(-33, -90) * mm, "end": v(-15, -108) * mm});
            skLineSegment(sketch, "E90.MirrorCS", {"start": v(-15, -108) * mm, "end": v(-15, -120) * mm});
            skArc(sketch, "E91.MirrorCS", {"start": v(15, -120) * mm, "mid": v(0, -135) * mm, "end": v(-15, -120) * mm});
            skLineSegment(sketch, "E92.MirrorCS", {"start": v(33, -90) * mm, "end": v(15, -108) * mm});
            skLineSegment(sketch, "E93.MirrorCS", {"start": v(15, -108) * mm, "end": v(15, -120) * mm});
            skLineSegment(sketch, "E94.MirrorCS", {"start": v(0, -90) * mm, "end": v(0, -120) * mm, "construction": true});
            skCircle(sketch, "E95.MirrorC", {"center": v(0, -120) * mm, "radius": 6 * mm});
            skSolve(sketch);
        }
        {
            var Q0;
            Q0 = qSketchRegion(id + "F16", true);
            var Q1;
            Q1=makeQuery(id+"F2.opExtrude","CAP_FACE",FACE,{"disambiguationData":[OSD([sQuery(id+"F0.wireOp",EDGE,"E12"),sQuery(id+"F0.wireOp",EDGE,"E13"),sQuery(id+"F0.wireOp",EDGE,"E14"),sQuery(id+"F0.wireOp",EDGE,"E15"),sQuery(id+"F0.wireOp",EDGE,"E17.filletArc"),sQuery(id+"F0.wireOp",EDGE,"E18.filletArc"),sQuery(id+"F0.wireOp",EDGE,"E19.filletArc"),sQuery(id+"F0.wireOp",EDGE,"E20.filletArc"),sQuery(id+"F0.wireOp",EDGE,"E25.0"),sQuery(id+"F0.wireOp",EDGE,"E25.1"),sQuery(id+"F0.wireOp",EDGE,"E25.2"),sQuery(id+"F0.wireOp",EDGE,"E25.3"),sQuery(id+"F0.wireOp",EDGE,"E25.4"),sQuery(id+"F0.wireOp",EDGE,"E25.5"),sQuery(id+"F0.wireOp",EDGE,"E25.6"),sQuery(id+"F0.wireOp",EDGE,"E25.7")])],"isStart":false});
            extrude(context, id + "F17", {"entities" : qUnion([Q0]), "endBound" : BoundingType.UP_TO_SURFACE, "depth" : 4 * mm, "endBoundEntityFace" : qUnion([Q1]), "offsetDistance" : 25 * mm});
        }
    });
